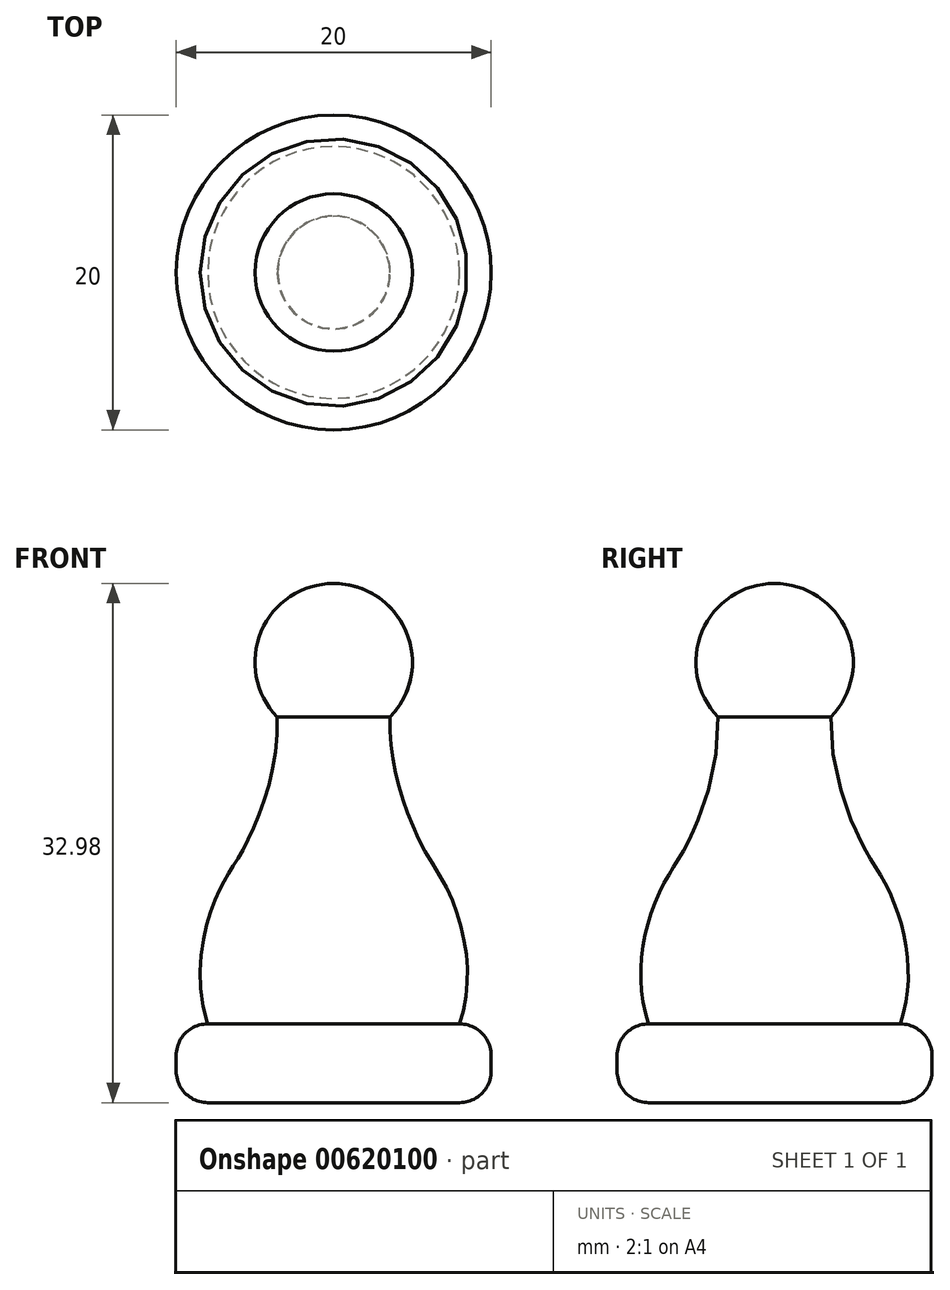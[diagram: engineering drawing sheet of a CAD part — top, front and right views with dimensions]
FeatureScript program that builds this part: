
annotation { "Feature Type Name" : "Feature", "Feature Type Description" : "" }
export const myFeature = defineFeature(function(context is Context, id is Id, definition is map)
    precondition{}
    {
        {
            var Q0;
            Q0=qCreatedBy(makeId("Front.planeOp"),FACE);
            var sketch = newSketch(context, id + "F0", { "sketchPlane" : qUnion([Q0])});
            skLineSegment(sketch, "E0", {"start": v(0, 0) * mm, "end": v(10, 0) * mm});
            skCircle(sketch, "E1", {"center": v(0, 27.98) * mm, "radius": 5 * mm});
            skLineSegment(sketch, "E2", {"start": v(10, 0) * mm, "end": v(10, 5) * mm});
            skLineSegment(sketch, "E3", {"start": v(10, 5) * mm, "end": v(8, 5) * mm});
            skLineSegment(sketch, "E4", {"start": v(0, 0) * mm, "end": v(0, 27.98) * mm});
            skLineSegment(sketch, "E5", {"start": v(0, 27.98) * mm, "end": v(0, 32.98) * mm});
            skFitSpline(sketch, "E6", {"points": [v(8, 5) * mm, v(7.31, 13.36) * mm, v(5.71, 16.15) * mm, v(3.59, 24.5) * mm], "startDerivative": vector(8.6, 26.09) * mm, "endDerivative": vector(1.05, 25.7) * mm});
            skLineSegment(sketch, "E7", {"start": v(4.78, 26.52) * mm, "end": v(-4.78, 26.52) * mm});
            skLineSegment(sketch, "E8", {"start": v(0, 27.98) * mm, "end": v(5, 27.98) * mm});
            skLineSegment(sketch, "E9", {"start": v(5, 27.98) * mm, "end": v(-5, 27.98) * mm});
            skSolve(sketch);
        }
        {
            var Q0;
            {var subQ4=sQuery(id+"F0.wireOp",EDGE,"E0");Q0=makeQuery(id+"F0.imprint","IMPRINT",FACE,{"disambiguationData":[TD([[makeQuery(id+"F0.imprint","IMPRINT",EDGE,{"derivedFrom":subQ4}),1.0]])]});}
            var Q1;
            {var subQ0=sQuery(id+"F0.wireOp",EDGE,"E1");var subQ1=makeQuery(id+"F0.imprint","INTERSECT",VERTEX,{"derivedFrom":[subQ0,sQuery(id+"F0.wireOp",EDGE,"E6")]});Q1=makeQuery(id+"F0.imprint","IMPRINT",FACE,{"disambiguationData":[TD([[makeQuery(id+"F0.imprint","IMPRINT",EDGE,{"disambiguationData":[TD([[subQ1,1.0]])],"derivedFrom":subQ0}),1.0]])]});}
            var Q2;
            {var subQ0=sQuery(id+"F0.wireOp",EDGE,"E7");var subQ1=sQuery(id+"F0.wireOp",EDGE,"E1");var subQ2=makeQuery(id+"F0.imprint","INTERSECT",VERTEX,{"disambiguationData":[OD(0.0)],"derivedFrom":[subQ1,subQ0]});Q2=makeQuery(id+"F0.imprint","IMPRINT",FACE,{"disambiguationData":[TD([[makeQuery(id+"F0.imprint","IMPRINT",EDGE,{"disambiguationData":[TD([[subQ2,-1.0]])],"derivedFrom":subQ1}),1.0]])]});}
            var Q3;
            {var subQ0=sQuery(id+"F0.wireOp",EDGE,"E5");Q3=makeQuery(id+"F0.imprint","IMPRINT",FACE,{"disambiguationData":[TD([[makeQuery(id+"F0.imprint","IMPRINT",EDGE,{"derivedFrom":subQ0}),-1.0]])]});}
            var Q4;
            Q4=sQuery(id+"F0.wireOp",EDGE,"E5");
            revolve(context, id + "F1", {"entities" : qUnion([Q0, Q1, Q2, Q3]), "axis" : qUnion([Q4]), "revolveType" : RevolveType.FULL});
        }
        {
            var Q0;
            Q0=makeQuery(id+"F1.opRevolve","SWEPT_EDGE",EDGE,{"disambiguationData":[OSD([sQuery(id+"F0.wireOp",EDGE,"E2"),sQuery(id+"F0.wireOp",EDGE,"E3")])]});
            fillet(context, id + "F2", {"entities" : qUnion([Q0]), "radius" : 2 * mm, "tangentPropagation" : true, "allowEdgeOverflow" : false});
        }
        {
            var Q0;
            Q0=makeQuery(id+"F1.opRevolve","SWEPT_EDGE",EDGE,{"disambiguationData":[OSD([sQuery(id+"F0.wireOp",EDGE,"E0"),sQuery(id+"F0.wireOp",EDGE,"E2")])]});
            fillet(context, id + "F3", {"entities" : qUnion([Q0]), "radius" : 2 * mm, "tangentPropagation" : true, "allowEdgeOverflow" : false});
        }
    });
